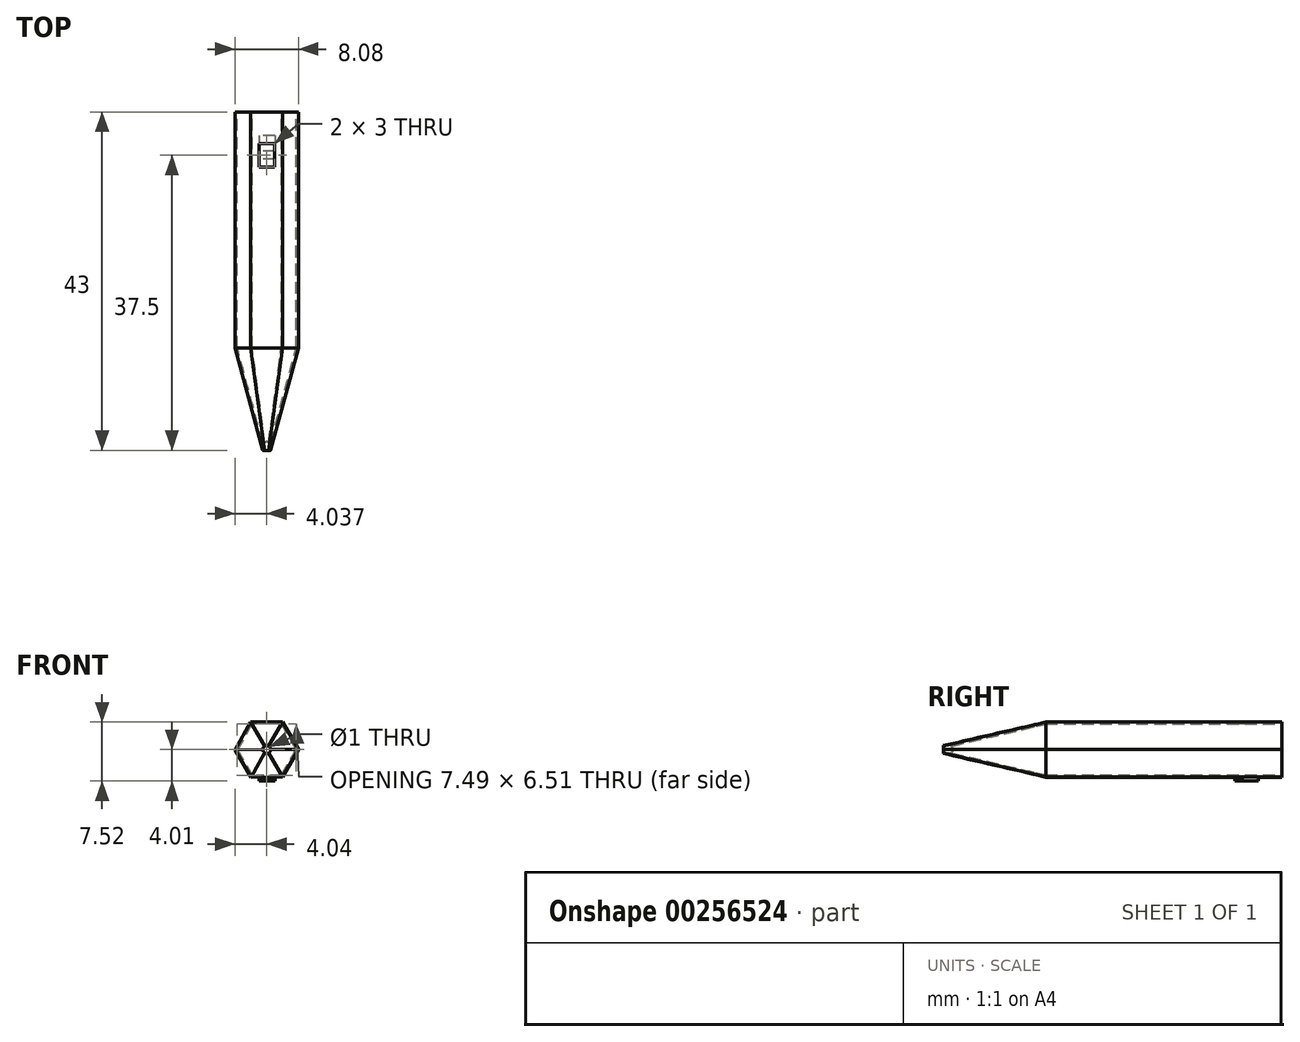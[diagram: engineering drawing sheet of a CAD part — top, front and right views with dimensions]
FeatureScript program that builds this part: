
annotation { "Feature Type Name" : "Feature", "Feature Type Description" : "" }
export const myFeature = defineFeature(function(context is Context, id is Id, definition is map)
    precondition{}
    {
        {
            var Q0;
            Q0=qCreatedBy(makeId("Front.planeOp"),FACE);
            cPlane(context, id + "F0", {"entities" : qUnion([Q0]), "cplaneType" : CPlaneType.OFFSET, "offset" : 13 * mm, "width" : 152.4 * mm, "height" : 152.4 * mm});
        }
        {
            var Q0;
            Q0=qCreatedBy(makeId("Front.planeOp"),FACE);
            var sketch = newSketch(context, id + "F1", { "sketchPlane" : qUnion([Q0])});
            skCircle(sketch, "E0", {"center": v(0, 0) * mm, "radius": 3.5 * mm, "construction": true});
            skLineSegment(sketch, "E1.0", {"start": v(-2, -3.51) * mm, "end": v(-4.04, -0.03) * mm});
            skLineSegment(sketch, "E1.1", {"start": v(-4.04, -0.03) * mm, "end": v(-2.04, 3.49) * mm});
            skLineSegment(sketch, "E1.2", {"start": v(-2.04, 3.49) * mm, "end": v(2, 3.51) * mm});
            skLineSegment(sketch, "E1.3", {"start": v(2, 3.51) * mm, "end": v(4.04, 0.03) * mm});
            skLineSegment(sketch, "E1.4", {"start": v(4.04, 0.03) * mm, "end": v(2.04, -3.49) * mm});
            skLineSegment(sketch, "E1.5", {"start": v(2.04, -3.49) * mm, "end": v(-2, -3.51) * mm});
            skPoint(sketch, "E1.0.midPoint", {"position": v(-3.02, -1.77) * mm});
            skSolve(sketch);
        }
        {
            var Q0;
            Q0=qCreatedBy(id+"F0.planeOp",FACE);
            var sketch = newSketch(context, id + "F2", { "sketchPlane" : qUnion([Q0])});
            skCircle(sketch, "E2", {"center": v(0, 0) * mm, "radius": 0.5 * mm});
            skSolve(sketch);
        }
        {
            var Q0;
            Q0=makeQuery(id+"F1.imprint","IMPRINT",FACE,{"disambiguationData":[TD([[makeQuery(id+"F1.imprint","IMPRINT",EDGE,{"derivedFrom":sQuery(id+"F1.wireOp",EDGE,"E1.0")}),-1.0]])]});
            var Q1;
            Q1=makeQuery(id+"F2.imprint","IMPRINT",FACE,{"disambiguationData":[TD([[makeQuery(id+"F2.imprint","IMPRINT",EDGE,{"derivedFrom":sQuery(id+"F2.wireOp",EDGE,"E2")}),1.0]])]});
            loft(context, id + "F3", {"sheetProfilesArray" : [{ "sheetProfileEntities" : qUnion([Q0]) }, { "sheetProfileEntities" : qUnion([Q1]) }]});
        }
        {
            var Q0;
            Q0=makeQuery(id+"F3.opLoft","CAP_FACE",FACE,{"disambiguationData":[OSD([makeQuery(id+"F1.imprint","IMPRINT",FACE,{"disambiguationData":[TD([[makeQuery(id+"F1.imprint","IMPRINT",EDGE,{"derivedFrom":sQuery(id+"F1.wireOp",EDGE,"E1.0")}),-1.0]])]})])],"isStart":true});
            extrude(context, id + "F4", {"entities" : qUnion([Q0]), "operationType" : NewBodyOperationType.ADD, "depth" : 30 * mm});
        }
        {
            var Q0;
            Q0=makeQuery(id+"F4.opExtrude","CAP_FACE",FACE,{"disambiguationData":[OSD([makeQuery(id+"F1.imprint","IMPRINT",FACE,{"disambiguationData":[TD([[makeQuery(id+"F1.imprint","IMPRINT",EDGE,{"derivedFrom":sQuery(id+"F1.wireOp",EDGE,"E1.0")}),-1.0]])]})])],"isStart":false});
            var sketch = newSketch(context, id + "F5", { "sketchPlane" : qUnion([Q0])});
            skLineSegment(sketch, "E3.0", {"start": v(3.75, -0.03) * mm, "end": v(1.85, -3.26) * mm});
            skLineSegment(sketch, "E3.1", {"start": v(-1.9, -3.24) * mm, "end": v(-3.75, 0.03) * mm});
            skLineSegment(sketch, "E3.2", {"start": v(-3.75, 0.03) * mm, "end": v(-1.85, 3.26) * mm});
            skLineSegment(sketch, "E3.3", {"start": v(1.85, -3.26) * mm, "end": v(-1.9, -3.24) * mm});
            skLineSegment(sketch, "E3.4", {"start": v(-1.85, 3.26) * mm, "end": v(1.9, 3.24) * mm});
            skLineSegment(sketch, "E3.5", {"start": v(1.9, 3.24) * mm, "end": v(3.75, -0.03) * mm});
            skSolve(sketch);
        }
        {
            var Q0;
            Q0=makeQuery(id+"F5.imprint","IMPRINT",FACE,{"disambiguationData":[TD([[makeQuery(id+"F5.imprint","IMPRINT",EDGE,{"derivedFrom":sQuery(id+"F5.wireOp",EDGE,"E3.0")}),-1.0]])]});
            extrude(context, id + "F6", {"entities" : qUnion([Q0]), "operationType" : NewBodyOperationType.REMOVE, "oppositeDirection" : true, "depth" : 30 * mm});
        }
        {
            var Q0;
            Q0=makeQuery(id+"F6.boolean.opBoolean","COPY",FACE,{"derivedFrom":makeQuery(id+"F6.opExtrude","CAP_FACE",FACE,{"disambiguationData":[OSD([makeQuery(id+"F1.imprint","IMPRINT",FACE,{"disambiguationData":[TD([[makeQuery(id+"F1.imprint","IMPRINT",EDGE,{"derivedFrom":sQuery(id+"F1.wireOp",EDGE,"E1.0")}),-1.0]])]}),sQuery(id+"F2.wireOp",EDGE,"E2"),sQuery(id+"F5.wireOp",EDGE,"E3.0"),sQuery(id+"F5.wireOp",EDGE,"E3.1"),sQuery(id+"F5.wireOp",EDGE,"E3.2"),sQuery(id+"F5.wireOp",EDGE,"E3.3"),sQuery(id+"F5.wireOp",EDGE,"E3.4"),sQuery(id+"F5.wireOp",EDGE,"E3.5")])],"isStart":false})});
            shell(context, id + "F7", {"entities" : qUnion([Q0]), "thickness" : 0.25 * mm});
        }
        {
            var Q0;
            Q0=makeQuery(id+"F2.imprint","IMPRINT",FACE,{"disambiguationData":[TD([[makeQuery(id+"F2.imprint","IMPRINT",EDGE,{"derivedFrom":sQuery(id+"F2.wireOp",EDGE,"E2")}),1.0]])]});
            extrude(context, id + "F8", {"entities" : qUnion([Q0]), "operationType" : NewBodyOperationType.REMOVE, "endBound" : BoundingType.THROUGH_ALL, "oppositeDirection" : true, "depth" : 25.4 * mm});
        }
        {
            var Q0;
            Q0=makeQuery(id+"F4.opExtrude","SWEPT_FACE",FACE,{"disambiguationData":[OSD([sQuery(id+"F1.wireOp",EDGE,"E1.1"),sQuery(id+"F1.wireOp",EDGE,"E1.2"),sQuery(id+"F1.wireOp",EDGE,"E1.3")])]});
            var sketch = newSketch(context, id + "F9", { "sketchPlane" : qUnion([Q0])});
            skLineSegment(sketch, "E4.bottom", {"start": v(-0.98, 23) * mm, "end": v(1.02, 23) * mm});
            skLineSegment(sketch, "E4.top", {"start": v(-0.98, 26) * mm, "end": v(1.02, 26) * mm});
            skLineSegment(sketch, "E4.left", {"start": v(-0.98, 23) * mm, "end": v(-0.98, 26) * mm});
            skLineSegment(sketch, "E4.right", {"start": v(1.02, 23) * mm, "end": v(1.02, 26) * mm});
            skSolve(sketch);
        }
        {
            var Q0;
            Q0=makeQuery(id+"F9.imprint","IMPRINT",FACE,{"disambiguationData":[TD([[makeQuery(id+"F9.imprint","IMPRINT",EDGE,{"derivedFrom":sQuery(id+"F9.wireOp",EDGE,"E4.bottom")}),1.0]])]});
            extrude(context, id + "F10", {"entities" : qUnion([Q0]), "operationType" : NewBodyOperationType.REMOVE, "oppositeDirection" : true, "depth" : 3.5 * mm});
        }
        {
            var Q0;
            Q0=makeQuery(id+"F4.opExtrude","SWEPT_FACE",FACE,{"disambiguationData":[OSD([sQuery(id+"F1.wireOp",EDGE,"E1.0"),sQuery(id+"F1.wireOp",EDGE,"E1.4"),sQuery(id+"F1.wireOp",EDGE,"E1.5")])]});
            var sketch = newSketch(context, id + "F11", { "sketchPlane" : qUnion([Q0])});
            skLineSegment(sketch, "E5.bottom", {"start": v(1.02, -27) * mm, "end": v(-0.98, -27) * mm});
            skLineSegment(sketch, "E5.top", {"start": v(1.02, -24) * mm, "end": v(-0.98, -24) * mm});
            skLineSegment(sketch, "E5.left", {"start": v(1.02, -27) * mm, "end": v(1.02, -24) * mm});
            skLineSegment(sketch, "E5.right", {"start": v(-0.98, -27) * mm, "end": v(-0.98, -24) * mm});
            skSolve(sketch);
        }
        {
            var Q0;
            Q0 = qSketchRegion(id + "F11", true);
            extrude(context, id + "F12", {"entities" : qUnion([Q0]), "operationType" : NewBodyOperationType.ADD, "depth" : 0.5 * mm});
        }
        {
            var Q0;
            Q0=makeQuery(id+"F12.opExtrude","SWEPT_FACE",FACE,{"disambiguationData":[OSD([sQuery(id+"F11.wireOp",EDGE,"E5.top")])]});
            var sketch = newSketch(context, id + "F13", { "sketchPlane" : qUnion([Q0])});
            skPoint(sketch, "E6.firstSnap0", {"position": v(1.05, -3.74) * mm});
            skLineSegment(sketch, "E6.bottom", {"start": v(1.05, -3.74) * mm, "end": v(-0.96, -3.74) * mm});
            skLineSegment(sketch, "E6.top", {"start": v(1.05, -3.5) * mm, "end": v(-0.96, -3.5) * mm});
            skLineSegment(sketch, "E6.left", {"start": v(1.05, -3.74) * mm, "end": v(1.05, -3.5) * mm});
            skLineSegment(sketch, "E6.right", {"start": v(-0.96, -3.74) * mm, "end": v(-0.96, -3.5) * mm});
            skSolve(sketch);
        }
        {
            var Q0;
            Q0 = qSketchRegion(id + "F13", true);
            extrude(context, id + "F14", {"entities" : qUnion([Q0]), "operationType" : NewBodyOperationType.REMOVE, "oppositeDirection" : true, "depth" : 1 * mm});
        }
    });
